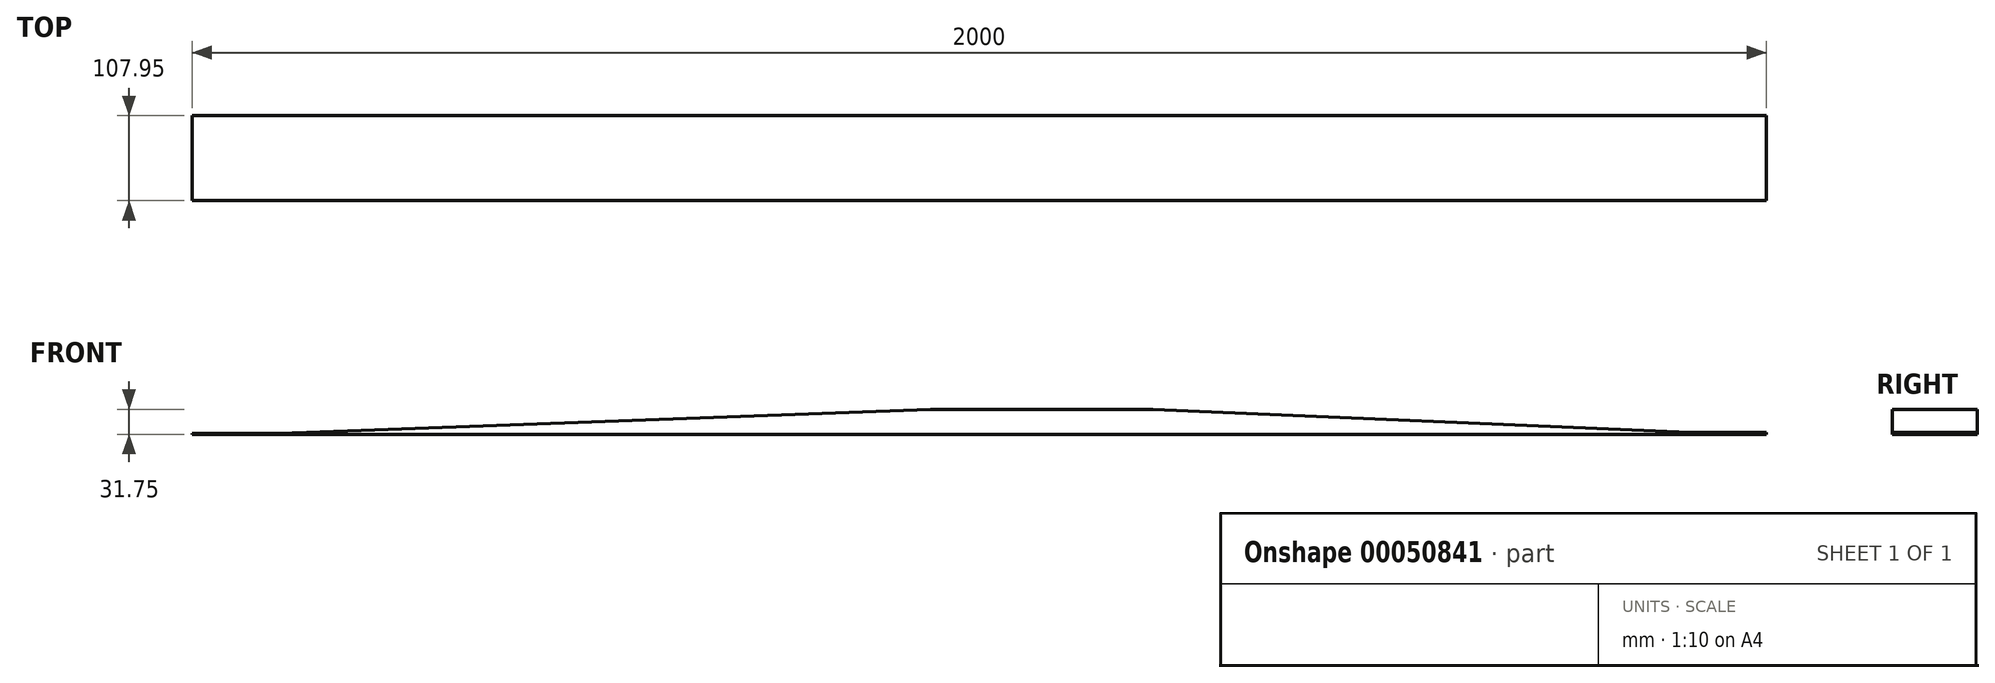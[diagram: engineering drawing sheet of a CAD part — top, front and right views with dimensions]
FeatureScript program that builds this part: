
annotation { "Feature Type Name" : "Feature", "Feature Type Description" : "" }
export const myFeature = defineFeature(function(context is Context, id is Id, definition is map)
    precondition{}
    {
        {
            var Q0;
            Q0=qCreatedBy(makeId("Front.planeOp"),FACE);
            var sketch = newSketch(context, id + "F0", { "sketchPlane" : qUnion([Q0])});
            skLineSegment(sketch, "E0", {"start": v(-1016, 0) * mm, "end": v(984, 0) * mm});
            skLineSegment(sketch, "E1", {"start": v(-76.2, 31.75) * mm, "end": v(203.2, 31.75) * mm});
            skLineSegment(sketch, "E2", {"start": v(-1016, 0) * mm, "end": v(-1016, 1.27) * mm});
            skLineSegment(sketch, "E3", {"start": v(-1016, 1.27) * mm, "end": v(-889, 1.27) * mm});
            skLineSegment(sketch, "E4", {"start": v(-889, 1.27) * mm, "end": v(-76.2, 31.75) * mm});
            skLineSegment(sketch, "E5", {"start": v(984, 0) * mm, "end": v(984, 2.03) * mm});
            skLineSegment(sketch, "E6", {"start": v(984, 2.03) * mm, "end": v(889, 2.03) * mm});
            skLineSegment(sketch, "E7", {"start": v(889, 2.03) * mm, "end": v(203.2, 31.75) * mm});
            skSolve(sketch);
        }
        {
            var Q0;
            Q0=makeQuery(id+"F0.imprint","IMPRINT",FACE,{"disambiguationData":[TD([[makeQuery(id+"F0.imprint","IMPRINT",EDGE,{"derivedFrom":sQuery(id+"F0.wireOp",EDGE,"E0")}),1.0]])]});
            extrude(context, id + "F1", {"entities" : qUnion([Q0]), "depth" : 107.95 * mm});
        }
        {
            var Q0;
            Q0=makeQuery(id+"F1.opExtrude","SWEPT_EDGE",EDGE,{"disambiguationData":[OSD([sQuery(id+"F0.wireOp",EDGE,"E3"),sQuery(id+"F0.wireOp",EDGE,"E4")])]});
            fillet(context, id + "F2", {"entities" : qUnion([Q0]), "radius" : 76.2 * mm, "tangentPropagation" : true, "allowEdgeOverflow" : false});
        }
        {
            var Q0;
            Q0=makeQuery(id+"F1.opExtrude","SWEPT_EDGE",EDGE,{"disambiguationData":[OSD([sQuery(id+"F0.wireOp",EDGE,"E1"),sQuery(id+"F0.wireOp",EDGE,"E4")])]});
            var Q1;
            Q1=makeQuery(id+"F1.opExtrude","SWEPT_EDGE",EDGE,{"disambiguationData":[OSD([sQuery(id+"F0.wireOp",EDGE,"E1"),sQuery(id+"F0.wireOp",EDGE,"E7")])]});
            var Q2;
            Q2=makeQuery(id+"F1.opExtrude","SWEPT_EDGE",EDGE,{"disambiguationData":[OSD([sQuery(id+"F0.wireOp",EDGE,"E6"),sQuery(id+"F0.wireOp",EDGE,"E7")])]});
            fillet(context, id + "F3", {"entities" : qUnion([Q0, Q1, Q2]), "radius" : 76.2 * mm, "tangentPropagation" : true, "allowEdgeOverflow" : false});
        }
    });
